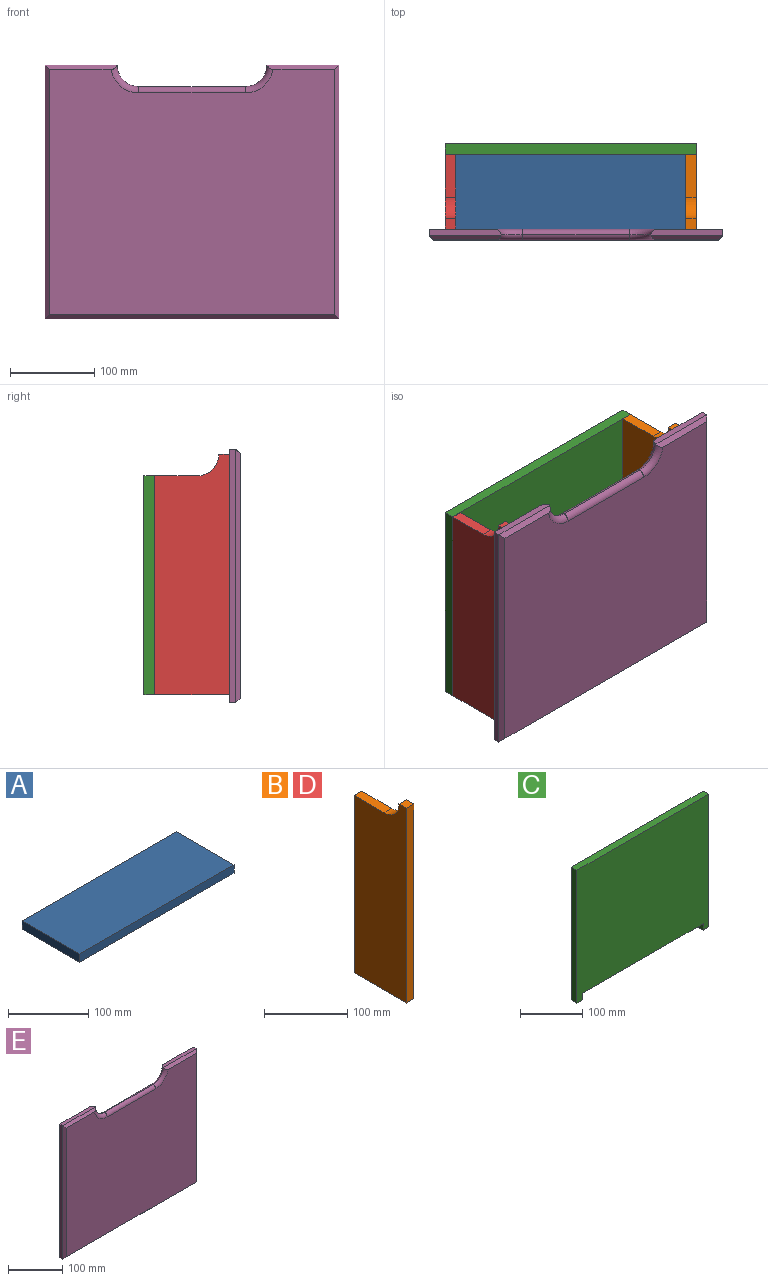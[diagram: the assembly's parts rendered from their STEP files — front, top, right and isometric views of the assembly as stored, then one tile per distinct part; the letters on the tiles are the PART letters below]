
ASSEMBLY  parts=5 mates=4
PART A: 6 faces, bbox 273.1x101.6x12.7 mm
  f0: plane 273.05x12.7mm, normal (0,1,0), area 3467.7mm2, adj f1,f3,f4,f5
  f1: plane 101.6x12.7mm, normal (-1,0,0), area 1290.3mm2, adj f0,f2,f4,f5
  f2: plane 273.05x12.7mm, normal (0,-1,0), area 3467.7mm2, adj f1,f3,f4,f5
  f3: plane 101.6x12.7mm, normal (1,0,0), area 1290.3mm2, adj f0,f2,f4,f5
  f4: plane 273.05x101.6mm, normal (0,0,1), area 27741.9mm2, adj f0,f1,f2,f3
  f5: plane 273.05x101.6mm, normal (0,0,-1), area 27741.9mm2, adj f0,f1,f2,f3
PART B: 8 faces, bbox 12.7x88.9x285.8 mm
  f0: plane 260.35x12.7mm, normal (0,1,0), area 3306.4mm2, adj f1,f5,f6,f7
  f1: plane 50.8x12.7mm, normal (0,0,1), area 645.2mm2, adj f0,f2,f6,f7
  f2: cylinder r=25.4mm len=25.4mm, axis (-1,0,0), area 506.7mm2, adj f1,f3,f6,f7
  f3: plane 12.7x12.7mm, normal (0,0,1), area 161.3mm2, adj f2,f4,f6,f7
  f4: plane 285.75x12.7mm, normal (0,-1,0), area 3629mm2, adj f3,f5,f6,f7
  f5: plane 88.9x12.7mm, normal (0,0,-1), area 1129mm2, adj f0,f4,f6,f7
  f6: plane 285.75x88.9mm, normal (1,0,0), area 23606.1mm2, adj f0,f1,f2,f3,f4,f5
  f7: plane 285.75x88.9mm, normal (-1,0,0), area 23606.1mm2, adj f0,f1,f2,f3,f4,f5
PART C: 10 faces, bbox 298.5x12.7x260.4 mm
  f0: plane 12.7x12.7mm, normal (1,0,0), area 161.3mm2, adj f1,f7,f8,f9
  f1: plane 273.05x12.7mm, normal (0,0,-1), area 3467.7mm2, adj f0,f2,f8,f9
  f2: plane 12.7x12.7mm, normal (-1,0,0), area 161.3mm2, adj f1,f3,f8,f9
  f3: plane 12.7x12.7mm, normal (0,0,-1), area 161.3mm2, adj f2,f4,f8,f9
  f4: plane 260.35x12.7mm, normal (1,0,0), area 3306.4mm2, adj f3,f5,f8,f9
  f5: plane 298.45x12.7mm, normal (0,0,1), area 3790.3mm2, adj f4,f6,f8,f9
  f6: plane 260.35x12.7mm, normal (-1,0,0), area 3306.4mm2, adj f5,f7,f8,f9
  f7: plane 12.7x12.7mm, normal (0,0,-1), area 161.3mm2, adj f0,f6,f8,f9
  f8: plane 298.45x260.35mm, normal (0,-1,0), area 74233.7mm2, adj f0,f1,f2,f3,f4,f5,f6,f7
  f9: plane 298.45x260.35mm, normal (0,1,0), area 74233.7mm2, adj f0,f1,f2,f3,f4,f5,f6,f7
PART D: same geometry as B
PART E: 18 faces, bbox 349.3x12.7x301.6 mm
  f0: plane 85.62x7.62mm, normal (0,0,1), area 640.5mm2, adj f4,f6,f11,f12,f13
  f1: plane 85.62x7.62mm, normal (0,0,1), area 640.5mm2, adj f2,f6,f7,f16,f17
  f2: plane 301.63x7.62mm, normal (-1,0,0), area 2298.4mm2, adj f1,f3,f6,f8
  f3: plane 349.25x7.62mm, normal (0,0,-1), area 2661.3mm2, adj f2,f4,f6,f9
  f4: plane 301.63x7.62mm, normal (1,0,0), area 2298.4mm2, adj f0,f3,f6,f10
  f5: plane 339.09x291.47mm, normal (0,-1,0), area 93906mm2, adj f7,f8,f9,f10,f11,f12,f14,f16
  f6: plane 349.25x301.63mm, normal (0,1,0), area 99436.3mm2, adj f0,f1,f2,f3,f4,f13,f15,f17
  f7: plane 85.29x5.08mm, normal (0,-0.71,0.71), area 581.6mm2, adj f1,f5,f8,f16
  f8: plane 301.63x5.08mm, normal (-0.71,-0.71,0), area 2130.4mm2, adj f2,f5,f7,f9
  f9: plane 349.25x5.08mm, normal (0,-0.71,-0.71), area 2472.6mm2, adj f3,f5,f8,f10
  f10: plane 301.63x5.08mm, normal (0.71,-0.71,0), area 2130.4mm2, adj f4,f5,f9,f11
  f11: plane 85.29x5.08mm, normal (0,-0.71,0.71), area 581.6mm2, adj f0,f5,f10,f12
  f12: torus R=33.02mm, axis (0,-1,0), area 447.6mm2, adj f0,f5,f11,f13,f14
  f13: torus R=33.02mm, axis (0,-1,0), area 478.6mm2, adj f0,f6,f12,f15
  f14: cylinder r=7.62mm len=127mm, axis (1,0,0), area 1358.1mm2, adj f5,f12,f15,f16
  f15: cylinder r=7.62mm len=127mm, axis (-1,0,0), area 1358.1mm2, adj f6,f13,f14,f17
  f16: torus R=33.02mm, axis (0,-1,0), area 447.6mm2, adj f1,f5,f7,f14,f17
  f17: torus R=33.02mm, axis (0,-1,0), area 478.6mm2, adj f1,f6,f15,f16
PLACE A t=(-442.73,-137.9,-165.6)mm
PLACE B t=(-237.02,199.29,135.47)mm
PLACE C t=(-413.49,114.3,-348.4)mm
PLACE D t=(-522.77,199.29,135.47)mm
PLACE E t=(-358.97,0,-9.53)mm
MATE fastened C.f0 <-> A.f1  axis (1,0,0) through (-510.07,101.6,-165.6)mm
MATE fastened D.f6 <-> A.f1  axis (1,0,0) through (-510.07,0,-165.6)mm
MATE fastened B.f7 <-> A.f3  axis (-1,0,0) through (-237.02,0,-165.6)mm
MATE fastened A.f2 <-> E.f6  axis (0,-1,0) through (-373.55,0,-165.6)mm
